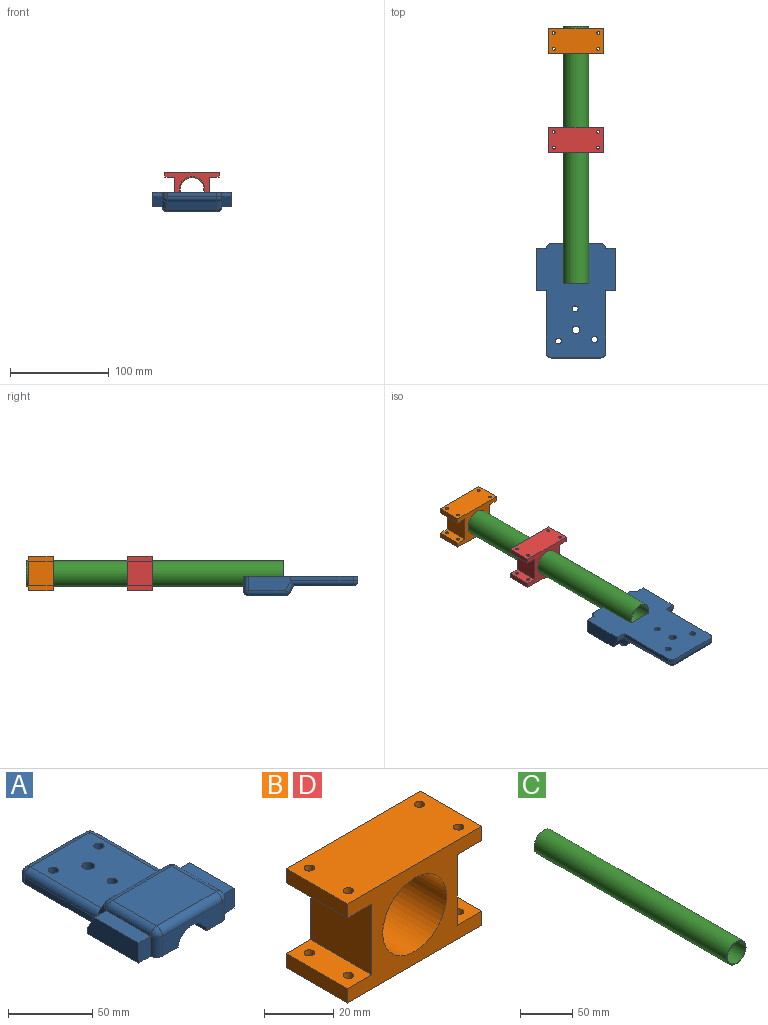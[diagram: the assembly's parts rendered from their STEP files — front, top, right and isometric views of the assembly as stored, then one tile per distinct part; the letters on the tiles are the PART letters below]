
ASSEMBLY  parts=4 mates=3
PART A: 45 faces, bbox 80x115.8x19.5 mm
  f0: plane 42.86x14.5mm, normal (-1,0,0), area 592.9mm2, adj f37,f38,f39,f41,f44
  f1: plane 42.86x14.5mm, normal (1,0,0), area 592.9mm2, adj f32,f33,f34,f36,f44
  f2: plane 50x4.54mm, normal (0,1,0), area 227mm2, adj f8,f9,f28,f44
  f3: plane 50x14.5mm, normal (0,-1,0), area 539.3mm2, adj f4,f6,f7,f17,f42,f43,f44
  f4: cylinder r=13mm len=40mm, axis (0,-1,0), area 1179.3mm2, adj f3,f5,f42,f43
  f5: plane 23.56x10mm, normal (0,-1,0), area 185.7mm2, adj f4,f42,f43,f44
  f6: cylinder r=5mm len=14.5mm, axis (0,0,1), area 113.9mm2, adj f3,f18,f32,f44
  f7: cylinder r=5mm len=14.5mm, axis (0,0,-1), area 113.9mm2, adj f3,f22,f37,f44
  f8: cylinder r=5mm len=5mm, axis (0,0,-1), area 35.7mm2, adj f2,f30,f35,f44
  f9: cylinder r=5mm len=5mm, axis (0,0,1), area 35.7mm2, adj f2,f31,f40,f44
  f10: cylinder r=3mm len=9.54mm, axis (0,0,-1), area 179.8mm2, adj f14,f44
  f11: cylinder r=3mm len=9.54mm, axis (0,0,-1), area 179.8mm2, adj f14,f44
  f12: cylinder r=3.78mm len=9.54mm, axis (0,0,-1), area 226.6mm2, adj f14,f44
  f13: cylinder r=3mm len=9.54mm, axis (0,0,-1), area 179.8mm2, adj f14,f44
  f14: plane 60x50mm, normal (0,0,1), area 2870.3mm2, adj f10,f11,f12,f13,f15,f27,f28,f29
  f15: plane 50x7.46mm, normal (0,0.87,0.5), area 430.7mm2, adj f14,f20,f25,f26
  f16: plane 50x37.11mm, normal (0,0,1), area 1855.7mm2, adj f17,f19,f20,f21
  f17: cylinder r=5mm len=50mm, axis (-1,0,0), area 392.7mm2, adj f3,f16,f18,f22
  f18: sphere r=5mm, area 39.3mm2, adj f6,f17,f19
  f19: cylinder r=5mm len=37.11mm, axis (0,1,0), area 291.5mm2, adj f16,f18,f23,f34
  f20: cylinder r=5mm len=50mm, axis (1,0,0), area 261.8mm2, adj f15,f16,f23,f24
  f21: cylinder r=5mm len=37.11mm, axis (0,-1,0), area 291.5mm2, adj f16,f22,f24,f38
  f22: sphere r=5mm, area 39.3mm2, adj f7,f17,f21
  f23: sphere r=5mm, area 26.2mm2, adj f19,f20,f25
  f24: sphere r=5mm, area 26.2mm2, adj f20,f21,f26
  f25: cylinder r=5mm len=12.46mm, axis (0,0.5,-0.87), area 75.9mm2, adj f15,f23,f27,f33
  f26: cylinder r=5mm len=12.46mm, axis (0,-0.5,0.87), area 75.9mm2, adj f15,f24,f29,f39
  f27: cylinder r=5mm len=62.89mm, axis (0,1,0), area 479.5mm2, adj f14,f25,f30,f35
  f28: cylinder r=5mm len=50mm, axis (-1,0,0), area 392.7mm2, adj f2,f14,f30,f31
  f29: cylinder r=5mm len=62.89mm, axis (0,-1,0), area 479.5mm2, adj f14,f26,f31,f40
  f30: sphere r=5mm, area 39.3mm2, adj f8,f27,f28
  f31: sphere r=5mm, area 39.3mm2, adj f9,f28,f29
  f32: plane 14.5x10mm, normal (0,-1,0), area 145mm2, adj f1,f6,f34,f44
  f33: plane 10x9.96mm, normal (0,0.87,0.5), area 115mm2, adj f1,f25,f34,f36
  f34: plane 37.11x10mm, normal (0,0,1), area 371.1mm2, adj f1,f19,f32,f33
  f35: plane 62.89x4.54mm, normal (1,0,0), area 285.6mm2, adj f8,f27,f36,f44
  f36: plane 10x4.54mm, normal (0,1,0), area 45.4mm2, adj f1,f33,f35,f44
  f37: plane 14.5x10mm, normal (0,-1,0), area 145mm2, adj f0,f7,f38,f44
  f38: plane 37.11x10mm, normal (0,0,1), area 371.1mm2, adj f0,f21,f37,f39
  f39: plane 10x9.96mm, normal (0,0.87,0.5), area 115mm2, adj f0,f26,f38,f41
  f40: plane 62.89x4.54mm, normal (-1,0,0), area 285.6mm2, adj f9,f29,f41,f44
  f41: plane 10x4.54mm, normal (0,1,0), area 45.4mm2, adj f0,f39,f40,f44
  f42: plane 40x2.5mm, normal (-1,0,0), area 100mm2, adj f3,f4,f5,f44
  f43: plane 40x2.5mm, normal (1,0,0), area 100mm2, adj f3,f4,f5,f44
  f44: plane 115.75x80mm, normal (0,0,-1), area 6708.8mm2, adj f0,f1,f2,f3,f5,f6,f7,f8
PART B: 23 faces, bbox 55x25x35 mm
  f0: plane 55x25mm, normal (0,0,1), area 1346.7mm2, adj f8,f9,f13,f14,f17,f18,f19,f20
  f1: plane 55x25mm, normal (0,0,-1), area 1346.7mm2, adj f6,f11,f13,f14,f15,f16,f21,f22
  f2: plane 25x10mm, normal (0,0,1), area 235.9mm2, adj f6,f7,f13,f14,f21,f22
  f3: plane 25x10mm, normal (0,0,-1), area 235.9mm2, adj f7,f8,f13,f14,f19,f20
  f4: plane 25x10mm, normal (0,0,-1), area 235.9mm2, adj f9,f10,f13,f14,f17,f18
  f5: plane 25x10mm, normal (0,0,1), area 235.9mm2, adj f10,f11,f13,f14,f15,f16
  f6: plane 25x5mm, normal (1,0,0), area 125mm2, adj f1,f2,f13,f14
  f7: plane 25x25mm, normal (1,0,0), area 625mm2, adj f2,f3,f13,f14
  f8: plane 25x5mm, normal (1,0,0), area 125mm2, adj f0,f3,f13,f14
  f9: plane 25x5mm, normal (-1,0,0), area 125mm2, adj f0,f4,f13,f14
  f10: plane 25x25mm, normal (-1,0,0), area 625mm2, adj f4,f5,f13,f14
  f11: plane 25x5mm, normal (-1,0,0), area 125mm2, adj f1,f5,f13,f14
  f12: cylinder r=13mm len=26mm, axis (0,1,0), area 2042mm2, adj f13,f14
  f13: plane 55x35mm, normal (0,-1,0), area 894.1mm2, adj f0,f1,f2,f3,f4,f5,f6,f7
  f14: plane 55x35mm, normal (0,1,0), area 894.1mm2, adj f0,f1,f2,f3,f4,f5,f6,f7
  f15: cylinder r=1.5mm len=5mm, axis (0,0,1), area 47.1mm2, adj f1,f5
  f16: cylinder r=1.5mm len=5mm, axis (0,0,1), area 47.1mm2, adj f1,f5
  f17: cylinder r=1.5mm len=5mm, axis (0,0,1), area 47.1mm2, adj f0,f4
  f18: cylinder r=1.5mm len=5mm, axis (0,0,1), area 47.1mm2, adj f0,f4
  f19: cylinder r=1.5mm len=5mm, axis (0,0,1), area 47.1mm2, adj f0,f3
  f20: cylinder r=1.5mm len=5mm, axis (0,0,1), area 47.1mm2, adj f0,f3
  f21: cylinder r=1.5mm len=5mm, axis (0,0,1), area 47.1mm2, adj f1,f2
  f22: cylinder r=1.5mm len=5mm, axis (0,0,1), area 47.1mm2, adj f1,f2
PART C: 4 faces, bbox 26x260x26 mm
  f0: cylinder r=12mm len=260mm, axis (0,1,0), area 19603.5mm2, adj f2,f3
  f1: cylinder r=13mm len=260mm, axis (0,1,0), area 21237.2mm2, adj f2,f3
  f2: plane 26x26mm, normal (0,-1,0), area 78.5mm2, adj f0,f1
  f3: plane 26x26mm, normal (0,1,0), area 78.5mm2, adj f0,f1
PART D: same geometry as B
PLACE A rot(axis=(1,0,0),180deg) t=(-7.25,-15.07,36.26)mm
PLACE B t=(-7.25,240.68,48.8)mm
PLACE C t=(-7.25,125.68,48.8)mm
PLACE D t=(-7.25,140.68,48.8)mm
MATE fastened B.f12 <-> C.f0  axis (0,1,0) through (-7.25,240.68,48.8)mm
MATE fastened D.f12 <-> C.f0  axis (0,1,0) through (-7.25,153.18,48.8)mm
MATE fastened A.f4 <-> C.f0  axis (0,1,0) through (-7.25,-4.32,48.8)mm
